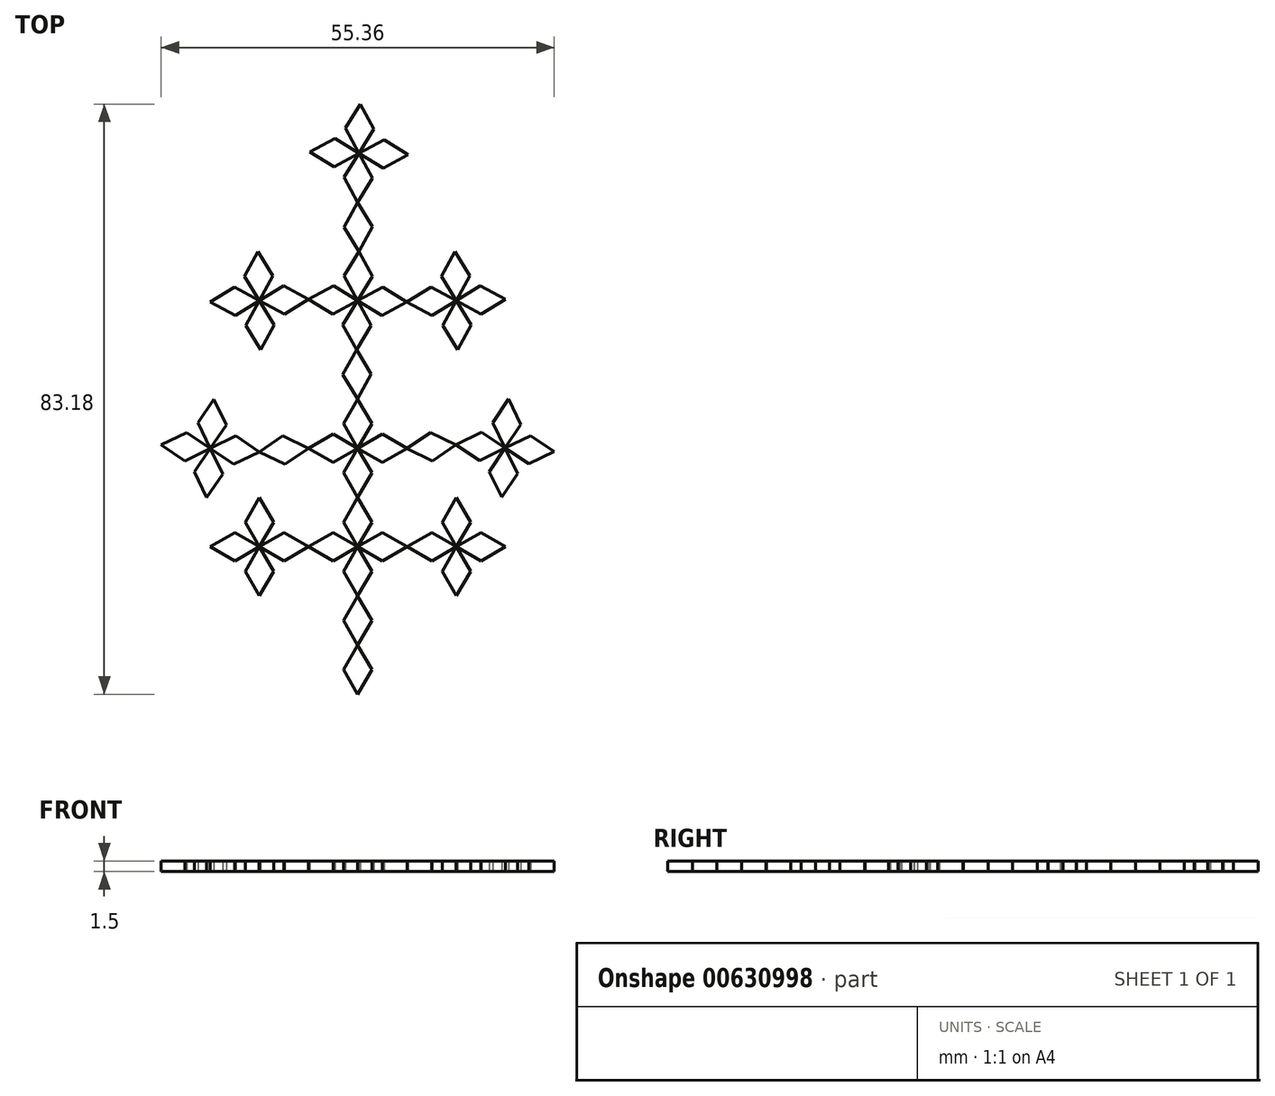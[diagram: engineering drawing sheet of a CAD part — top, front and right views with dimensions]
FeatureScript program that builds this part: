
annotation { "Feature Type Name" : "Feature", "Feature Type Description" : "" }
export const myFeature = defineFeature(function(context is Context, id is Id, definition is map)
    precondition{}
    {
        {
            var Q0;
            Q0=qCreatedBy(makeId("Top.planeOp"),FACE);
            var sketch = newSketch(context, id + "F0", { "sketchPlane" : qUnion([Q0])});
            skLineSegment(sketch, "E0.0", {"start": v(0, 6.93) * mm, "end": v(2, 3.46) * mm});
            skLineSegment(sketch, "E0.2", {"start": v(-2, 3.46) * mm, "end": v(0, 6.93) * mm});
            skLineSegment(sketch, "E1.MirrorCS", {"start": v(-2, 3.46) * mm, "end": v(0, 0) * mm});
            skLineSegment(sketch, "E2.MirrorCS", {"start": v(0, 0) * mm, "end": v(2, 3.46) * mm});
            skLineSegment(sketch, "E3.1.0", {"start": v(-3.46, -2) * mm, "end": v(-6.93, 0) * mm});
            skLineSegment(sketch, "E3.1.1", {"start": v(0, 0) * mm, "end": v(-3.46, 2) * mm});
            skLineSegment(sketch, "E3.1.2", {"start": v(-6.93, 0) * mm, "end": v(-3.46, 2) * mm});
            skLineSegment(sketch, "E3.1.3", {"start": v(-3.46, -2) * mm, "end": v(0, 0) * mm});
            skLineSegment(sketch, "E3.2.0", {"start": v(2, -3.46) * mm, "end": v(0, -6.93) * mm});
            skLineSegment(sketch, "E3.2.1", {"start": v(0, 0) * mm, "end": v(-2, -3.46) * mm});
            skLineSegment(sketch, "E3.2.2", {"start": v(0, -6.93) * mm, "end": v(-2, -3.46) * mm});
            skLineSegment(sketch, "E3.2.3", {"start": v(2, -3.46) * mm, "end": v(0, 0) * mm});
            skLineSegment(sketch, "E3.3.0", {"start": v(3.46, 2) * mm, "end": v(6.93, 0) * mm});
            skLineSegment(sketch, "E3.3.1", {"start": v(0, 0) * mm, "end": v(3.46, -2) * mm});
            skLineSegment(sketch, "E3.3.2", {"start": v(6.93, 0) * mm, "end": v(3.46, -2) * mm});
            skLineSegment(sketch, "E3.3.3", {"start": v(3.46, 2) * mm, "end": v(0, 0) * mm});
            skPoint(sketch, "E3.center", {"position": v(0, 0) * mm});
            skLineSegment(sketch, "E4.0", {"start": v(0, 6.93) * mm, "end": v(-2, 10.4) * mm});
            skLineSegment(sketch, "E4.2", {"start": v(2, 10.4) * mm, "end": v(0, 6.93) * mm});
            skLineSegment(sketch, "E5.MirrorCS", {"start": v(2, 10.4) * mm, "end": v(0, 13.86) * mm});
            skLineSegment(sketch, "E6.MirrorCS", {"start": v(0, 13.86) * mm, "end": v(-2, 10.4) * mm});
            skLineSegment(sketch, "E7.1.0", {"start": v(3.46, 15.86) * mm, "end": v(6.93, 13.86) * mm});
            skLineSegment(sketch, "E7.1.1", {"start": v(0, 13.86) * mm, "end": v(3.46, 11.86) * mm});
            skLineSegment(sketch, "E7.1.2", {"start": v(6.93, 13.86) * mm, "end": v(3.46, 11.86) * mm});
            skLineSegment(sketch, "E7.1.3", {"start": v(3.46, 15.86) * mm, "end": v(0, 13.86) * mm});
            skLineSegment(sketch, "E7.2.0", {"start": v(-2, 17.32) * mm, "end": v(0, 20.78) * mm});
            skLineSegment(sketch, "E7.2.1", {"start": v(0, 13.86) * mm, "end": v(2, 17.32) * mm});
            skLineSegment(sketch, "E7.2.2", {"start": v(0, 20.78) * mm, "end": v(2, 17.32) * mm});
            skLineSegment(sketch, "E7.2.3", {"start": v(-2, 17.32) * mm, "end": v(0, 13.86) * mm});
            skLineSegment(sketch, "E7.3.0", {"start": v(-3.46, 11.86) * mm, "end": v(-6.93, 13.86) * mm});
            skLineSegment(sketch, "E7.3.1", {"start": v(0, 13.86) * mm, "end": v(-3.46, 15.86) * mm});
            skLineSegment(sketch, "E7.3.2", {"start": v(-6.93, 13.86) * mm, "end": v(-3.46, 15.86) * mm});
            skLineSegment(sketch, "E7.3.3", {"start": v(-3.46, 11.86) * mm, "end": v(0, 13.86) * mm});
            skPoint(sketch, "E7.center", {"position": v(0, 13.86) * mm});
            skLineSegment(sketch, "E8.MirrorCS", {"start": v(-10.4, -2) * mm, "end": v(-6.93, 0) * mm});
            skLineSegment(sketch, "E9.MirrorCS", {"start": v(-6.93, 0) * mm, "end": v(-10.4, 2) * mm});
            skLineSegment(sketch, "E10.MirrorCS", {"start": v(-13.86, 0) * mm, "end": v(-10.4, 2) * mm});
            skLineSegment(sketch, "E11.MirrorCS", {"start": v(-10.4, -2) * mm, "end": v(-13.86, 0) * mm});
            skLineSegment(sketch, "E12.1.0", {"start": v(-13.86, 0) * mm, "end": v(-15.86, 3.46) * mm});
            skLineSegment(sketch, "E12.1.1", {"start": v(-11.86, 3.46) * mm, "end": v(-13.86, 6.93) * mm});
            skLineSegment(sketch, "E12.1.2", {"start": v(-13.86, 6.93) * mm, "end": v(-15.86, 3.46) * mm});
            skLineSegment(sketch, "E12.1.3", {"start": v(-11.86, 3.46) * mm, "end": v(-13.86, 0) * mm});
            skLineSegment(sketch, "E12.2.0", {"start": v(-13.86, 0) * mm, "end": v(-17.32, -2) * mm});
            skLineSegment(sketch, "E12.2.1", {"start": v(-17.32, 2) * mm, "end": v(-20.78, 0) * mm});
            skLineSegment(sketch, "E12.2.2", {"start": v(-20.78, 0) * mm, "end": v(-17.32, -2) * mm});
            skLineSegment(sketch, "E12.2.3", {"start": v(-17.32, 2) * mm, "end": v(-13.86, 0) * mm});
            skLineSegment(sketch, "E12.3.0", {"start": v(-13.86, 0) * mm, "end": v(-11.86, -3.46) * mm});
            skLineSegment(sketch, "E12.3.1", {"start": v(-15.86, -3.46) * mm, "end": v(-13.86, -6.93) * mm});
            skLineSegment(sketch, "E12.3.2", {"start": v(-13.86, -6.93) * mm, "end": v(-11.86, -3.46) * mm});
            skLineSegment(sketch, "E12.3.3", {"start": v(-15.86, -3.46) * mm, "end": v(-13.86, 0) * mm});
            skPoint(sketch, "E12.center", {"position": v(-13.86, 0) * mm});
            skPoint(sketch, "E0.cCircle.center.orphan", {"position": v(0, 4.62) * mm});
            skSolve(sketch);
        }
        {
            var Q0;
            Q0=qCreatedBy(makeId("Top.planeOp"),FACE);
            var sketch = newSketch(context, id + "F1", { "sketchPlane" : qUnion([Q0])});
            skLineSegment(sketch, "E13.0", {"start": v(0, 20.83) * mm, "end": v(-2.1, 24.23) * mm});
            skLineSegment(sketch, "E13.2", {"start": v(1.9, 24.34) * mm, "end": v(0, 20.83) * mm});
            skLineSegment(sketch, "E14.MirrorCS", {"start": v(-0.19, 27.75) * mm, "end": v(-2.1, 24.23) * mm});
            skLineSegment(sketch, "E15.MirrorCS", {"start": v(1.9, 24.34) * mm, "end": v(-0.19, 27.75) * mm});
            skLineSegment(sketch, "E16.0", {"start": v(0, -13.88) * mm, "end": v(-2, -10.41) * mm});
            skLineSegment(sketch, "E16.2", {"start": v(2, -10.41) * mm, "end": v(0, -13.88) * mm});
            skLineSegment(sketch, "E17.MirrorCS", {"start": v(0, -6.95) * mm, "end": v(-2, -10.41) * mm});
            skLineSegment(sketch, "E18.MirrorCS", {"start": v(2, -10.41) * mm, "end": v(0, -6.95) * mm});
            skLineSegment(sketch, "E19.MirrorCS", {"start": v(-0.19, 27.75) * mm, "end": v(-2.1, 31.27) * mm});
            skLineSegment(sketch, "E20.MirrorCS", {"start": v(1.9, 31.16) * mm, "end": v(-0.19, 27.75) * mm});
            skLineSegment(sketch, "E21.MirrorCS", {"start": v(0, 34.68) * mm, "end": v(-2.1, 31.27) * mm});
            skLineSegment(sketch, "E22.MirrorCS", {"start": v(1.9, 31.16) * mm, "end": v(0, 34.68) * mm});
            skLineSegment(sketch, "E23.1.0", {"start": v(3.52, 36.58) * mm, "end": v(6.93, 34.49) * mm});
            skLineSegment(sketch, "E23.1.1", {"start": v(3.52, 36.58) * mm, "end": v(0, 34.68) * mm});
            skLineSegment(sketch, "E23.1.2", {"start": v(6.93, 34.49) * mm, "end": v(3.4, 32.58) * mm});
            skLineSegment(sketch, "E23.1.3", {"start": v(0, 34.68) * mm, "end": v(3.4, 32.58) * mm});
            skLineSegment(sketch, "E23.2.0", {"start": v(-1.9, 38.2) * mm, "end": v(0.19, 41.6) * mm});
            skLineSegment(sketch, "E23.2.1", {"start": v(-1.9, 38.2) * mm, "end": v(0, 34.68) * mm});
            skLineSegment(sketch, "E23.2.2", {"start": v(0.19, 41.6) * mm, "end": v(2.1, 38.09) * mm});
            skLineSegment(sketch, "E23.2.3", {"start": v(0, 34.68) * mm, "end": v(2.1, 38.09) * mm});
            skLineSegment(sketch, "E23.3.0", {"start": v(-3.52, 32.77) * mm, "end": v(-6.93, 34.87) * mm});
            skLineSegment(sketch, "E23.3.1", {"start": v(-3.52, 32.77) * mm, "end": v(0, 34.68) * mm});
            skLineSegment(sketch, "E23.3.2", {"start": v(-6.93, 34.87) * mm, "end": v(-3.4, 36.77) * mm});
            skLineSegment(sketch, "E23.3.3", {"start": v(0, 34.68) * mm, "end": v(-3.4, 36.77) * mm});
            skPoint(sketch, "E23.center", {"position": v(0, 34.68) * mm});
            skLineSegment(sketch, "E24.MirrorCS", {"start": v(-1.9, 45.01) * mm, "end": v(0.19, 41.6) * mm});
            skLineSegment(sketch, "E25.MirrorCS", {"start": v(-1.9, 45.01) * mm, "end": v(0, 48.53) * mm});
            skLineSegment(sketch, "E26.MirrorCS", {"start": v(0, 48.53) * mm, "end": v(2.1, 45.12) * mm});
            skLineSegment(sketch, "E27.MirrorCS", {"start": v(0.19, 41.6) * mm, "end": v(2.1, 45.12) * mm});
            skLineSegment(sketch, "E28.MirrorCS", {"start": v(-6.93, 34.87) * mm, "end": v(-10.44, 36.77) * mm});
            skLineSegment(sketch, "E29.MirrorCS", {"start": v(-10.33, 32.77) * mm, "end": v(-6.93, 34.87) * mm});
            skLineSegment(sketch, "E30.MirrorCS", {"start": v(-10.33, 32.77) * mm, "end": v(-13.85, 34.68) * mm});
            skLineSegment(sketch, "E31.MirrorCS", {"start": v(-13.85, 34.68) * mm, "end": v(-10.44, 36.77) * mm});
            skLineSegment(sketch, "E32.1.0", {"start": v(-13.85, 34.68) * mm, "end": v(-15.94, 38.09) * mm});
            skLineSegment(sketch, "E32.1.1", {"start": v(-14.04, 41.6) * mm, "end": v(-15.94, 38.09) * mm});
            skLineSegment(sketch, "E32.1.2", {"start": v(-11.95, 38.2) * mm, "end": v(-13.85, 34.68) * mm});
            skLineSegment(sketch, "E32.1.3", {"start": v(-11.95, 38.2) * mm, "end": v(-14.04, 41.6) * mm});
            skLineSegment(sketch, "E32.2.0", {"start": v(-13.85, 34.68) * mm, "end": v(-17.26, 32.58) * mm});
            skLineSegment(sketch, "E32.2.1", {"start": v(-20.78, 34.49) * mm, "end": v(-17.26, 32.58) * mm});
            skLineSegment(sketch, "E32.2.2", {"start": v(-17.37, 36.58) * mm, "end": v(-13.85, 34.68) * mm});
            skLineSegment(sketch, "E32.2.3", {"start": v(-17.37, 36.58) * mm, "end": v(-20.78, 34.49) * mm});
            skLineSegment(sketch, "E32.3.0", {"start": v(-13.85, 34.68) * mm, "end": v(-11.76, 31.27) * mm});
            skLineSegment(sketch, "E32.3.1", {"start": v(-13.66, 27.75) * mm, "end": v(-11.76, 31.27) * mm});
            skLineSegment(sketch, "E32.3.2", {"start": v(-15.76, 31.16) * mm, "end": v(-13.85, 34.68) * mm});
            skLineSegment(sketch, "E32.3.3", {"start": v(-15.76, 31.16) * mm, "end": v(-13.66, 27.75) * mm});
            skPoint(sketch, "E32.center", {"position": v(-13.85, 34.68) * mm});
            skLineSegment(sketch, "E33.MirrorCS", {"start": v(10.33, 36.58) * mm, "end": v(6.93, 34.49) * mm});
            skLineSegment(sketch, "E34.MirrorCS", {"start": v(6.93, 34.49) * mm, "end": v(10.44, 32.58) * mm});
            skLineSegment(sketch, "E35.MirrorCS", {"start": v(13.85, 34.68) * mm, "end": v(10.44, 32.58) * mm});
            skLineSegment(sketch, "E36.MirrorCS", {"start": v(10.33, 36.58) * mm, "end": v(13.85, 34.68) * mm});
            skLineSegment(sketch, "E37.1.0", {"start": v(14.04, 27.75) * mm, "end": v(15.94, 31.27) * mm});
            skLineSegment(sketch, "E37.1.1", {"start": v(11.95, 31.16) * mm, "end": v(14.04, 27.75) * mm});
            skLineSegment(sketch, "E37.1.2", {"start": v(11.95, 31.16) * mm, "end": v(13.85, 34.68) * mm});
            skLineSegment(sketch, "E37.1.3", {"start": v(13.85, 34.68) * mm, "end": v(15.94, 31.27) * mm});
            skLineSegment(sketch, "E37.2.0", {"start": v(20.78, 34.87) * mm, "end": v(17.26, 36.77) * mm});
            skLineSegment(sketch, "E37.2.1", {"start": v(17.37, 32.77) * mm, "end": v(20.78, 34.87) * mm});
            skLineSegment(sketch, "E37.2.2", {"start": v(17.37, 32.77) * mm, "end": v(13.85, 34.68) * mm});
            skLineSegment(sketch, "E37.2.3", {"start": v(13.85, 34.68) * mm, "end": v(17.26, 36.77) * mm});
            skLineSegment(sketch, "E37.3.0", {"start": v(13.66, 41.6) * mm, "end": v(11.76, 38.09) * mm});
            skLineSegment(sketch, "E37.3.1", {"start": v(15.76, 38.2) * mm, "end": v(13.66, 41.6) * mm});
            skLineSegment(sketch, "E37.3.2", {"start": v(15.76, 38.2) * mm, "end": v(13.85, 34.68) * mm});
            skLineSegment(sketch, "E37.3.3", {"start": v(13.85, 34.68) * mm, "end": v(11.76, 38.09) * mm});
            skPoint(sketch, "E37.center", {"position": v(13.85, 34.68) * mm});
            skLineSegment(sketch, "E38.MirrorCS", {"start": v(-1.9, 52.05) * mm, "end": v(0, 48.53) * mm});
            skLineSegment(sketch, "E39.MirrorCS", {"start": v(0, 48.53) * mm, "end": v(2.1, 51.94) * mm});
            skLineSegment(sketch, "E40.MirrorCS", {"start": v(0.19, 55.45) * mm, "end": v(2.1, 51.94) * mm});
            skLineSegment(sketch, "E41.MirrorCS", {"start": v(-1.9, 52.05) * mm, "end": v(0.19, 55.45) * mm});
            skLineSegment(sketch, "E42.1.0", {"start": v(3.6, 53.36) * mm, "end": v(7.11, 55.27) * mm});
            skLineSegment(sketch, "E42.1.1", {"start": v(0.19, 55.45) * mm, "end": v(3.7, 57.36) * mm});
            skLineSegment(sketch, "E42.1.2", {"start": v(7.11, 55.27) * mm, "end": v(3.7, 57.36) * mm});
            skLineSegment(sketch, "E42.1.3", {"start": v(3.6, 53.36) * mm, "end": v(0.19, 55.45) * mm});
            skLineSegment(sketch, "E42.2.0", {"start": v(2.28, 58.86) * mm, "end": v(0.38, 62.38) * mm});
            skLineSegment(sketch, "E42.2.1", {"start": v(0.19, 55.45) * mm, "end": v(-1.72, 58.97) * mm});
            skLineSegment(sketch, "E42.2.2", {"start": v(0.38, 62.38) * mm, "end": v(-1.72, 58.97) * mm});
            skLineSegment(sketch, "E42.2.3", {"start": v(2.28, 58.86) * mm, "end": v(0.19, 55.45) * mm});
            skLineSegment(sketch, "E42.3.0", {"start": v(-3.22, 57.55) * mm, "end": v(-6.74, 55.64) * mm});
            skLineSegment(sketch, "E42.3.1", {"start": v(0.19, 55.45) * mm, "end": v(-3.33, 53.55) * mm});
            skLineSegment(sketch, "E42.3.2", {"start": v(-6.74, 55.64) * mm, "end": v(-3.33, 53.55) * mm});
            skLineSegment(sketch, "E42.3.3", {"start": v(-3.22, 57.55) * mm, "end": v(0.19, 55.45) * mm});
            skPoint(sketch, "E42.center", {"position": v(0.19, 55.45) * mm});
            skLineSegment(sketch, "E43.MirrorCS", {"start": v(2, -17.34) * mm, "end": v(0, -13.88) * mm});
            skLineSegment(sketch, "E44.MirrorCS", {"start": v(0, -13.88) * mm, "end": v(-2, -17.34) * mm});
            skLineSegment(sketch, "E45.MirrorCS", {"start": v(0, -20.8) * mm, "end": v(-2, -17.34) * mm});
            skLineSegment(sketch, "E46.MirrorCS", {"start": v(2, -17.34) * mm, "end": v(0, -20.8) * mm});
            skPoint(sketch, "E16.cCircle.center.orphan", {"position": v(0, -11.57) * mm});
            skPoint(sketch, "E47.start.orphan", {"position": v(-1.71, 27.75) * mm});
            skSolve(sketch);
        }
        {
            var Q0;
            Q0=qCreatedBy(makeId("Top.planeOp"),FACE);
            var sketch = newSketch(context, id + "F2", { "sketchPlane" : qUnion([Q0])});
            skLineSegment(sketch, "E48.0", {"start": v(-6.96, 13.85) * mm, "end": v(-10.27, 11.6) * mm});
            skLineSegment(sketch, "E48.2", {"start": v(-10.56, 15.6) * mm, "end": v(-6.96, 13.85) * mm});
            skLineSegment(sketch, "E49.MirrorCS", {"start": v(-10.56, 15.6) * mm, "end": v(-13.87, 13.36) * mm});
            skLineSegment(sketch, "E50.MirrorCS", {"start": v(-13.87, 13.36) * mm, "end": v(-10.27, 11.6) * mm});
            skArc(sketch, "E51.cCircle", {"start": v(13.84, 14.2) * mm, "mid": v(13.84, 14.27) * mm, "end": v(13.83, 14.35) * mm, "construction": true});
            skLineSegment(sketch, "E51.0", {"start": v(13.83, 14.35) * mm, "end": v(10.53, 12.1) * mm});
            skLineSegment(sketch, "E51.2", {"start": v(10.23, 16.1) * mm, "end": v(13.83, 14.35) * mm});
            skLineSegment(sketch, "E52.MirrorCS", {"start": v(10.23, 16.1) * mm, "end": v(6.92, 13.84) * mm});
            skLineSegment(sketch, "E53.MirrorCS", {"start": v(6.92, 13.84) * mm, "end": v(10.53, 12.1) * mm});
            skPoint(sketch, "E54.endSnap0", {"position": v(-13.87, 12.95) * mm});
            skLineSegment(sketch, "E55.MirrorCS", {"start": v(-17.18, 15.6) * mm, "end": v(-13.87, 13.36) * mm});
            skLineSegment(sketch, "E56.MirrorCS", {"start": v(-13.87, 13.36) * mm, "end": v(-17.47, 11.6) * mm});
            skLineSegment(sketch, "E57.MirrorCS", {"start": v(-17.18, 15.6) * mm, "end": v(-20.78, 13.85) * mm});
            skLineSegment(sketch, "E58.MirrorCS", {"start": v(-20.78, 13.85) * mm, "end": v(-17.47, 11.6) * mm});
            skLineSegment(sketch, "E59.1.0", {"start": v(-22.53, 17.45) * mm, "end": v(-20.29, 20.76) * mm});
            skLineSegment(sketch, "E59.1.1", {"start": v(-20.29, 20.76) * mm, "end": v(-18.54, 17.16) * mm});
            skLineSegment(sketch, "E59.1.2", {"start": v(-20.78, 13.85) * mm, "end": v(-18.54, 17.16) * mm});
            skLineSegment(sketch, "E59.1.3", {"start": v(-22.53, 17.45) * mm, "end": v(-20.78, 13.85) * mm});
            skLineSegment(sketch, "E59.2.0", {"start": v(-24.38, 12.1) * mm, "end": v(-27.7, 14.34) * mm});
            skLineSegment(sketch, "E59.2.1", {"start": v(-27.7, 14.34) * mm, "end": v(-24.1, 16.1) * mm});
            skLineSegment(sketch, "E59.2.2", {"start": v(-20.78, 13.85) * mm, "end": v(-24.1, 16.1) * mm});
            skLineSegment(sketch, "E59.2.3", {"start": v(-24.38, 12.1) * mm, "end": v(-20.78, 13.85) * mm});
            skLineSegment(sketch, "E59.3.0", {"start": v(-19.03, 10.25) * mm, "end": v(-21.27, 6.94) * mm});
            skLineSegment(sketch, "E59.3.1", {"start": v(-21.27, 6.94) * mm, "end": v(-23.02, 10.54) * mm});
            skLineSegment(sketch, "E59.3.2", {"start": v(-20.78, 13.85) * mm, "end": v(-23.02, 10.54) * mm});
            skLineSegment(sketch, "E59.3.3", {"start": v(-19.03, 10.25) * mm, "end": v(-20.78, 13.85) * mm});
            skPoint(sketch, "E59.center", {"position": v(-20.78, 13.85) * mm});
            skLineSegment(sketch, "E60.MirrorCS", {"start": v(17.44, 16.12) * mm, "end": v(13.85, 14.35) * mm});
            skLineSegment(sketch, "E61.MirrorCS", {"start": v(13.85, 14.35) * mm, "end": v(17.17, 12.13) * mm});
            skLineSegment(sketch, "E62.MirrorCS", {"start": v(20.76, 13.9) * mm, "end": v(17.17, 12.13) * mm});
            skLineSegment(sketch, "E63.MirrorCS", {"start": v(17.44, 16.12) * mm, "end": v(20.76, 13.9) * mm});
            skLineSegment(sketch, "E64.1.0", {"start": v(20.76, 13.9) * mm, "end": v(22.52, 10.3) * mm});
            skLineSegment(sketch, "E64.1.1", {"start": v(20.3, 6.98) * mm, "end": v(22.52, 10.3) * mm});
            skLineSegment(sketch, "E64.1.2", {"start": v(18.53, 10.57) * mm, "end": v(20.3, 6.98) * mm});
            skLineSegment(sketch, "E64.1.3", {"start": v(18.53, 10.57) * mm, "end": v(20.76, 13.9) * mm});
            skLineSegment(sketch, "E64.2.0", {"start": v(20.76, 13.9) * mm, "end": v(24.35, 15.66) * mm});
            skLineSegment(sketch, "E64.2.1", {"start": v(27.67, 13.43) * mm, "end": v(24.35, 15.66) * mm});
            skLineSegment(sketch, "E64.2.2", {"start": v(24.08, 11.67) * mm, "end": v(27.67, 13.43) * mm});
            skLineSegment(sketch, "E64.2.3", {"start": v(24.08, 11.67) * mm, "end": v(20.76, 13.9) * mm});
            skLineSegment(sketch, "E64.3.0", {"start": v(20.76, 13.9) * mm, "end": v(19, 17.48) * mm});
            skLineSegment(sketch, "E64.3.1", {"start": v(21.22, 20.8) * mm, "end": v(19, 17.48) * mm});
            skLineSegment(sketch, "E64.3.2", {"start": v(22.98, 17.22) * mm, "end": v(21.22, 20.8) * mm});
            skLineSegment(sketch, "E64.3.3", {"start": v(22.98, 17.22) * mm, "end": v(20.76, 13.9) * mm});
            skPoint(sketch, "E64.center", {"position": v(20.76, 13.9) * mm});
            skPoint(sketch, "E65.start.orphan", {"position": v(13.83, 15.88) * mm});
            skPoint(sketch, "E66.orphan", {"position": v(-13.87, 12.53) * mm});
            skPoint(sketch, "E54.end.orphan", {"position": v(-13.87, 13.98) * mm});
            skSolve(sketch);
        }
        {
            var Q0;
            Q0=qCreatedBy(makeId("Top.planeOp"),FACE);
            var sketch = newSketch(context, id + "F3", { "sketchPlane" : qUnion([Q0])});
            skLineSegment(sketch, "E67.0", {"start": v(13.89, 0) * mm, "end": v(10.42, -2) * mm});
            skLineSegment(sketch, "E67.2", {"start": v(10.42, 2) * mm, "end": v(13.89, 0) * mm});
            skLineSegment(sketch, "E68.MirrorCS", {"start": v(10.42, 2) * mm, "end": v(6.96, 0) * mm});
            skLineSegment(sketch, "E69.MirrorCS", {"start": v(6.96, 0) * mm, "end": v(10.42, -2) * mm});
            skLineSegment(sketch, "E70.1.0", {"start": v(11.89, -3.46) * mm, "end": v(13.89, -6.93) * mm});
            skLineSegment(sketch, "E70.1.1", {"start": v(13.89, 0) * mm, "end": v(15.89, -3.46) * mm});
            skLineSegment(sketch, "E70.1.2", {"start": v(13.89, -6.93) * mm, "end": v(15.89, -3.46) * mm});
            skLineSegment(sketch, "E70.1.3", {"start": v(11.89, -3.46) * mm, "end": v(13.89, 0) * mm});
            skLineSegment(sketch, "E70.2.0", {"start": v(17.35, -2) * mm, "end": v(20.82, 0) * mm});
            skLineSegment(sketch, "E70.2.1", {"start": v(13.89, 0) * mm, "end": v(17.35, 2) * mm});
            skLineSegment(sketch, "E70.2.2", {"start": v(20.82, 0) * mm, "end": v(17.35, 2) * mm});
            skLineSegment(sketch, "E70.2.3", {"start": v(17.35, -2) * mm, "end": v(13.89, 0) * mm});
            skLineSegment(sketch, "E70.3.0", {"start": v(15.89, 3.46) * mm, "end": v(13.89, 6.93) * mm});
            skLineSegment(sketch, "E70.3.1", {"start": v(13.89, 0) * mm, "end": v(11.89, 3.46) * mm});
            skLineSegment(sketch, "E70.3.2", {"start": v(13.89, 6.93) * mm, "end": v(11.89, 3.46) * mm});
            skLineSegment(sketch, "E70.3.3", {"start": v(15.89, 3.46) * mm, "end": v(13.89, 0) * mm});
            skPoint(sketch, "E70.center", {"position": v(13.89, 0) * mm});
            skPoint(sketch, "E67.cCircle.center.orphan", {"position": v(11.58, 0) * mm});
            skSolve(sketch);
        }
        {
            var Q0;
            Q0=makeQuery(id+"F1.imprint","IMPRINT",FACE,{"disambiguationData":[TD([[makeQuery(id+"F1.imprint","IMPRINT",EDGE,{"derivedFrom":sQuery(id+"F1.wireOp",EDGE,"E43.MirrorCS")}),1.0]])]});
            var Q1;
            Q1=makeQuery(id+"F1.imprint","IMPRINT",FACE,{"disambiguationData":[TD([[makeQuery(id+"F1.imprint","IMPRINT",EDGE,{"derivedFrom":sQuery(id+"F1.wireOp",EDGE,"E16.0")}),-1.0]])]});
            var Q2;
            Q2=makeQuery(id+"F0.imprint","IMPRINT",FACE,{"disambiguationData":[TD([[makeQuery(id+"F0.imprint","IMPRINT",EDGE,{"derivedFrom":sQuery(id+"F0.wireOp",EDGE,"E3.2.0")}),-1.0]])]});
            var Q3;
            Q3=makeQuery(id+"F0.imprint","IMPRINT",FACE,{"disambiguationData":[TD([[makeQuery(id+"F0.imprint","IMPRINT",EDGE,{"derivedFrom":sQuery(id+"F0.wireOp",EDGE,"E3.3.0")}),-1.0]])]});
            var Q4;
            Q4=makeQuery(id+"F0.imprint","IMPRINT",FACE,{"disambiguationData":[TD([[makeQuery(id+"F0.imprint","IMPRINT",EDGE,{"derivedFrom":sQuery(id+"F0.wireOp",EDGE,"E0.0")}),-1.0]])]});
            var Q5;
            Q5=makeQuery(id+"F0.imprint","IMPRINT",FACE,{"disambiguationData":[TD([[makeQuery(id+"F0.imprint","IMPRINT",EDGE,{"derivedFrom":sQuery(id+"F0.wireOp",EDGE,"E3.1.0")}),-1.0]])]});
            var Q6;
            Q6=makeQuery(id+"F3.imprint","IMPRINT",FACE,{"disambiguationData":[TD([[makeQuery(id+"F3.imprint","IMPRINT",EDGE,{"derivedFrom":sQuery(id+"F3.wireOp",EDGE,"E67.0")}),-1.0]])]});
            var Q7;
            Q7=makeQuery(id+"F3.imprint","IMPRINT",FACE,{"disambiguationData":[TD([[makeQuery(id+"F3.imprint","IMPRINT",EDGE,{"derivedFrom":sQuery(id+"F3.wireOp",EDGE,"E70.3.0")}),1.0]])]});
            var Q8;
            Q8=makeQuery(id+"F3.imprint","IMPRINT",FACE,{"disambiguationData":[TD([[makeQuery(id+"F3.imprint","IMPRINT",EDGE,{"derivedFrom":sQuery(id+"F3.wireOp",EDGE,"E70.2.0")}),1.0]])]});
            var Q9;
            Q9=makeQuery(id+"F3.imprint","IMPRINT",FACE,{"disambiguationData":[TD([[makeQuery(id+"F3.imprint","IMPRINT",EDGE,{"derivedFrom":sQuery(id+"F3.wireOp",EDGE,"E70.1.0")}),1.0]])]});
            var Q10;
            Q10=makeQuery(id+"F0.imprint","IMPRINT",FACE,{"disambiguationData":[TD([[makeQuery(id+"F0.imprint","IMPRINT",EDGE,{"derivedFrom":sQuery(id+"F0.wireOp",EDGE,"E8.MirrorCS")}),1.0]])]});
            var Q11;
            Q11=makeQuery(id+"F0.imprint","IMPRINT",FACE,{"disambiguationData":[TD([[makeQuery(id+"F0.imprint","IMPRINT",EDGE,{"derivedFrom":sQuery(id+"F0.wireOp",EDGE,"E12.3.0")}),-1.0]])]});
            var Q12;
            Q12=makeQuery(id+"F0.imprint","IMPRINT",FACE,{"disambiguationData":[TD([[makeQuery(id+"F0.imprint","IMPRINT",EDGE,{"derivedFrom":sQuery(id+"F0.wireOp",EDGE,"E12.2.0")}),-1.0]])]});
            var Q13;
            Q13=makeQuery(id+"F0.imprint","IMPRINT",FACE,{"disambiguationData":[TD([[makeQuery(id+"F0.imprint","IMPRINT",EDGE,{"derivedFrom":sQuery(id+"F0.wireOp",EDGE,"E12.1.0")}),-1.0]])]});
            var Q14;
            Q14=makeQuery(id+"F0.imprint","IMPRINT",FACE,{"disambiguationData":[TD([[makeQuery(id+"F0.imprint","IMPRINT",EDGE,{"derivedFrom":sQuery(id+"F0.wireOp",EDGE,"E4.0")}),-1.0]])]});
            var Q15;
            Q15=makeQuery(id+"F0.imprint","IMPRINT",FACE,{"disambiguationData":[TD([[makeQuery(id+"F0.imprint","IMPRINT",EDGE,{"derivedFrom":sQuery(id+"F0.wireOp",EDGE,"E7.1.0")}),-1.0]])]});
            var Q16;
            Q16=makeQuery(id+"F0.imprint","IMPRINT",FACE,{"disambiguationData":[TD([[makeQuery(id+"F0.imprint","IMPRINT",EDGE,{"derivedFrom":sQuery(id+"F0.wireOp",EDGE,"E7.2.0")}),-1.0]])]});
            var Q17;
            Q17=makeQuery(id+"F0.imprint","IMPRINT",FACE,{"disambiguationData":[TD([[makeQuery(id+"F0.imprint","IMPRINT",EDGE,{"derivedFrom":sQuery(id+"F0.wireOp",EDGE,"E7.3.0")}),-1.0]])]});
            var Q18;
            Q18=makeQuery(id+"F2.imprint","IMPRINT",FACE,{"disambiguationData":[TD([[makeQuery(id+"F2.imprint","IMPRINT",EDGE,{"derivedFrom":sQuery(id+"F2.wireOp",EDGE,"E51.0")}),-1.0]])]});
            var Q19;
            Q19=makeQuery(id+"F2.imprint","IMPRINT",FACE,{"disambiguationData":[TD([[makeQuery(id+"F2.imprint","IMPRINT",EDGE,{"derivedFrom":sQuery(id+"F2.wireOp",EDGE,"E60.MirrorCS")}),1.0]])]});
            var Q20;
            Q20=makeQuery(id+"F2.imprint","IMPRINT",FACE,{"disambiguationData":[TD([[makeQuery(id+"F2.imprint","IMPRINT",EDGE,{"derivedFrom":sQuery(id+"F2.wireOp",EDGE,"E64.1.0")}),-1.0]])]});
            var Q21;
            Q21=makeQuery(id+"F2.imprint","IMPRINT",FACE,{"disambiguationData":[TD([[makeQuery(id+"F2.imprint","IMPRINT",EDGE,{"derivedFrom":sQuery(id+"F2.wireOp",EDGE,"E64.2.0")}),-1.0]])]});
            var Q22;
            Q22=makeQuery(id+"F2.imprint","IMPRINT",FACE,{"disambiguationData":[TD([[makeQuery(id+"F2.imprint","IMPRINT",EDGE,{"derivedFrom":sQuery(id+"F2.wireOp",EDGE,"E64.3.0")}),-1.0]])]});
            var Q23;
            Q23=makeQuery(id+"F2.imprint","IMPRINT",FACE,{"disambiguationData":[TD([[makeQuery(id+"F2.imprint","IMPRINT",EDGE,{"derivedFrom":sQuery(id+"F2.wireOp",EDGE,"E48.0")}),-1.0]])]});
            var Q24;
            Q24=makeQuery(id+"F2.imprint","IMPRINT",FACE,{"disambiguationData":[TD([[makeQuery(id+"F2.imprint","IMPRINT",EDGE,{"derivedFrom":sQuery(id+"F2.wireOp",EDGE,"E55.MirrorCS")}),-1.0]])]});
            var Q25;
            Q25=makeQuery(id+"F2.imprint","IMPRINT",FACE,{"disambiguationData":[TD([[makeQuery(id+"F2.imprint","IMPRINT",EDGE,{"derivedFrom":sQuery(id+"F2.wireOp",EDGE,"E59.3.0")}),-1.0]])]});
            var Q26;
            Q26=makeQuery(id+"F2.imprint","IMPRINT",FACE,{"disambiguationData":[TD([[makeQuery(id+"F2.imprint","IMPRINT",EDGE,{"derivedFrom":sQuery(id+"F2.wireOp",EDGE,"E59.2.0")}),-1.0]])]});
            var Q27;
            Q27=makeQuery(id+"F2.imprint","IMPRINT",FACE,{"disambiguationData":[TD([[makeQuery(id+"F2.imprint","IMPRINT",EDGE,{"derivedFrom":sQuery(id+"F2.wireOp",EDGE,"E59.1.0")}),-1.0]])]});
            var Q28;
            Q28=makeQuery(id+"F1.imprint","IMPRINT",FACE,{"disambiguationData":[TD([[makeQuery(id+"F1.imprint","IMPRINT",EDGE,{"derivedFrom":sQuery(id+"F1.wireOp",EDGE,"E13.0")}),-1.0]])]});
            var Q29;
            Q29=makeQuery(id+"F1.imprint","IMPRINT",FACE,{"disambiguationData":[TD([[makeQuery(id+"F1.imprint","IMPRINT",EDGE,{"derivedFrom":sQuery(id+"F1.wireOp",EDGE,"E19.MirrorCS")}),-1.0]])]});
            var Q30;
            Q30=makeQuery(id+"F1.imprint","IMPRINT",FACE,{"disambiguationData":[TD([[makeQuery(id+"F1.imprint","IMPRINT",EDGE,{"derivedFrom":sQuery(id+"F1.wireOp",EDGE,"E23.1.0")}),-1.0]])]});
            var Q31;
            Q31=makeQuery(id+"F1.imprint","IMPRINT",FACE,{"disambiguationData":[TD([[makeQuery(id+"F1.imprint","IMPRINT",EDGE,{"derivedFrom":sQuery(id+"F1.wireOp",EDGE,"E23.2.0")}),-1.0]])]});
            var Q32;
            Q32=makeQuery(id+"F1.imprint","IMPRINT",FACE,{"disambiguationData":[TD([[makeQuery(id+"F1.imprint","IMPRINT",EDGE,{"derivedFrom":sQuery(id+"F1.wireOp",EDGE,"E23.3.0")}),-1.0]])]});
            var Q33;
            Q33=makeQuery(id+"F1.imprint","IMPRINT",FACE,{"disambiguationData":[TD([[makeQuery(id+"F1.imprint","IMPRINT",EDGE,{"derivedFrom":sQuery(id+"F1.wireOp",EDGE,"E33.MirrorCS")}),1.0]])]});
            var Q34;
            Q34=makeQuery(id+"F1.imprint","IMPRINT",FACE,{"disambiguationData":[TD([[makeQuery(id+"F1.imprint","IMPRINT",EDGE,{"derivedFrom":sQuery(id+"F1.wireOp",EDGE,"E37.1.0")}),1.0]])]});
            var Q35;
            Q35=makeQuery(id+"F1.imprint","IMPRINT",FACE,{"disambiguationData":[TD([[makeQuery(id+"F1.imprint","IMPRINT",EDGE,{"derivedFrom":sQuery(id+"F1.wireOp",EDGE,"E37.2.0")}),1.0]])]});
            var Q36;
            Q36=makeQuery(id+"F1.imprint","IMPRINT",FACE,{"disambiguationData":[TD([[makeQuery(id+"F1.imprint","IMPRINT",EDGE,{"derivedFrom":sQuery(id+"F1.wireOp",EDGE,"E37.3.0")}),1.0]])]});
            var Q37;
            Q37=makeQuery(id+"F1.imprint","IMPRINT",FACE,{"disambiguationData":[TD([[makeQuery(id+"F1.imprint","IMPRINT",EDGE,{"derivedFrom":sQuery(id+"F1.wireOp",EDGE,"E24.MirrorCS")}),1.0]])]});
            var Q38;
            Q38=makeQuery(id+"F1.imprint","IMPRINT",FACE,{"disambiguationData":[TD([[makeQuery(id+"F1.imprint","IMPRINT",EDGE,{"derivedFrom":sQuery(id+"F1.wireOp",EDGE,"E38.MirrorCS")}),1.0]])]});
            var Q39;
            Q39=makeQuery(id+"F1.imprint","IMPRINT",FACE,{"disambiguationData":[TD([[makeQuery(id+"F1.imprint","IMPRINT",EDGE,{"derivedFrom":sQuery(id+"F1.wireOp",EDGE,"E42.1.0")}),1.0]])]});
            var Q40;
            Q40=makeQuery(id+"F1.imprint","IMPRINT",FACE,{"disambiguationData":[TD([[makeQuery(id+"F1.imprint","IMPRINT",EDGE,{"derivedFrom":sQuery(id+"F1.wireOp",EDGE,"E42.2.0")}),1.0]])]});
            var Q41;
            Q41=makeQuery(id+"F1.imprint","IMPRINT",FACE,{"disambiguationData":[TD([[makeQuery(id+"F1.imprint","IMPRINT",EDGE,{"derivedFrom":sQuery(id+"F1.wireOp",EDGE,"E42.3.0")}),1.0]])]});
            var Q42;
            Q42=makeQuery(id+"F1.imprint","IMPRINT",FACE,{"disambiguationData":[TD([[makeQuery(id+"F1.imprint","IMPRINT",EDGE,{"derivedFrom":sQuery(id+"F1.wireOp",EDGE,"E32.3.0")}),-1.0]])]});
            var Q43;
            Q43=makeQuery(id+"F1.imprint","IMPRINT",FACE,{"disambiguationData":[TD([[makeQuery(id+"F1.imprint","IMPRINT",EDGE,{"derivedFrom":sQuery(id+"F1.wireOp",EDGE,"E28.MirrorCS")}),1.0]])]});
            var Q44;
            Q44=makeQuery(id+"F1.imprint","IMPRINT",FACE,{"disambiguationData":[TD([[makeQuery(id+"F1.imprint","IMPRINT",EDGE,{"derivedFrom":sQuery(id+"F1.wireOp",EDGE,"E32.1.0")}),-1.0]])]});
            var Q45;
            Q45=makeQuery(id+"F1.imprint","IMPRINT",FACE,{"disambiguationData":[TD([[makeQuery(id+"F1.imprint","IMPRINT",EDGE,{"derivedFrom":sQuery(id+"F1.wireOp",EDGE,"E32.2.0")}),-1.0]])]});
            extrude(context, id + "F4", {"entities" : qUnion([Q0, Q1, Q2, Q3, Q4, Q5, Q6, Q7, Q8, Q9, Q10, Q11, Q12, Q13, Q14, Q15, Q16, Q17, Q18, Q19, Q20, Q21, Q22, Q23, Q24, Q25, Q26, Q27, Q28, Q29, Q30, Q31, Q32, Q33, Q34, Q35, Q36, Q37, Q38, Q39, Q40, Q41, Q42, Q43, Q44, Q45]), "depth" : 1.5 * mm, "offsetDistance" : 25 * mm});
        }
    });
